# Revit family: JMv 315 - 630
name_source: partatom
category: Mechanical Equipment
revit_build: Autodesk Revit MEP 2014 (Build: 20130308_1515(x64)
units: mm (PartAtom-declared; Revit-internal decimal feet)

## types (49) — shared parameters
Air Flow Rate Supply = 0 m³/h
Blade Angle = 0.00°
Description = 0000 JM
Electrical Load (Input Power) = 0 kW
Electrical Power (Rated Power) = 0 kW
Fan Code = Model/code
Fan Diameter / Size = 0000 mm
Frequency = 50 Hz
Full Load Current = 0 A
Manufacturer = Flakt Woods Group
Material = Steel
Max Voltage = 420 V
Maximum Operating Temperature = 60 °C
Min Voltage = 380 V
Minimum Operating Temperature = -20 °C
Model = Model/code
Motor Rating = 0 kW
Mounting Feet = Yes
Organisation = Flakt Woods Group
Power = 0 kW
Protective Earth = No
Smoke Control Flow rate Extract = 0 m³/h
Smoke Control Temperature = 0 °C
Smoke Control Time = 0.0 min
Starting Current = 0 A
T/Box 12 O'clock = Yes
T/Box 3 O'clock = No
T/Box 9 O'clock = No
Total Pressure Supply = 0.00 Pa
URL = http://www.flaktwoods.com
zero-valued in all types: Annual Carbon Footprint, Blades, Breakout Sound Level - Lw dB(A), Cost, Extract Diameter, Fan Speed - RPM, Inlet Sound Level - Lw dB(A), Outlet Sound Level - Lw dB(A), Overall Height, Poles, SFP - W/(l/s), Size, Unit Height, Unit Width

## per-type parameters (varying)
| type | Dimension D | Dimension K | Dimension L | Dimension L/2 | Dimension P | Fan Radius | Feet Extrusion Start | Flange Holes | Flange Size | Hub | Overall Length | Overall Width | Smoke Control Flow rate Supply | Static Pressure Supply | Supply Diameter | Total Weight | Unit Length | Unit Weight | Velocity Supply |
| 315 BT4 | 230 mm | 285 mm  [stored 0.935039 ft] | 265 mm  [stored 0.869423 ft] | 133 mm | 200 mm  [stored 0.656168 ft] | 158 mm | -158 mm |  | 40 mm  [stored 0.131234 ft] | 0 | 1565 mm | 45 mm  [stored 0.147638 ft] | 0 m³/h | 0.00 Pa | 315 mm  [stored 1.03346 ft] | 0.00 kg | 375 mm  [stored 1.23031 ft] | 20.78 kg | 0 m/s |
| 315 BT5 | 230 mm | 285 mm  [stored 0.935039 ft] | 265 mm  [stored 0.869423 ft] | 133 mm | 200 mm  [stored 0.656168 ft] | 158 mm | -158 mm |  | 40 mm  [stored 0.131234 ft] | 0 | 1565 mm | 45 mm  [stored 0.147638 ft] | 0 m³/h | 0.00 Pa | 315 mm  [stored 1.03346 ft] | 0.00 kg | 375 mm  [stored 1.23031 ft] | 21.28 kg | 0 m/s |
| 315 BT9 | 230 mm | 285 mm  [stored 0.935039 ft] | 265 mm  [stored 0.869423 ft] | 133 mm | 200 mm  [stored 0.656168 ft] | 158 mm | -158 mm |  | 40 mm  [stored 0.131234 ft] | 0 | 1565 mm | 45 mm  [stored 0.147638 ft] | 0 m³/h | 0.00 Pa | 315 mm  [stored 1.03346 ft] | 0.00 kg | 375 mm  [stored 1.23031 ft] | 22.78 kg | 0 m/s |
| 315 CT5 | 230 mm | 285 mm  [stored 0.935039 ft] | 265 mm  [stored 0.869423 ft] | 133 mm | 200 mm  [stored 0.656168 ft] | 158 mm | -158 mm |  | 40 mm  [stored 0.131234 ft] | 0 | 1565 mm | 45 mm  [stored 0.147638 ft] | 0 m³/h | 0.00 Pa | 315 mm  [stored 1.03346 ft] | 0.00 kg | 375 mm  [stored 1.23031 ft] | 23.76 kg | 0 m/s |
| 315 CT9 | 230 mm | 285 mm  [stored 0.935039 ft] | 265 mm  [stored 0.869423 ft] | 133 mm | 200 mm  [stored 0.656168 ft] | 158 mm | -158 mm |  | 40 mm  [stored 0.131234 ft] | 0 | 1565 mm | 45 mm  [stored 0.147638 ft] | 0 m³/h | 0.00 Pa | 315 mm  [stored 1.03346 ft] | 0.00 kg | 375 mm  [stored 1.23031 ft] | 26.76 kg | 0 m/s |
| 315 80 | 230 mm | 285 mm  [stored 0.935039 ft] | 265 mm  [stored 0.869423 ft] | 133 mm | 200 mm  [stored 0.656168 ft] | 158 mm | -158 mm |  | 40 mm  [stored 0.131234 ft] | 0 | 1565 mm | 45 mm  [stored 0.147638 ft] | 0 m³/h | 0.00 Pa | 315 mm  [stored 1.03346 ft] | 0.00 kg | 375 mm  [stored 1.23031 ft] | 32.52 kg | 0 m/s |
| 355 BT4 | 250 mm  [stored 0.82021 ft] | 285 mm  [stored 0.935039 ft] | 305 mm  [stored 1.00066 ft] | 153 mm | 225 mm  [stored 0.738189 ft] | 178 mm | -178 mm |  | 40 mm  [stored 0.131234 ft] | 0 | 1565 mm | 45 mm  [stored 0.147638 ft] | 0 m³/h | 0.00 Pa | 355 mm | 0.00 kg | 375 mm  [stored 1.23031 ft] | 22.18 kg | 0 m/s |
| 355 BT5 | 250 mm  [stored 0.82021 ft] | 285 mm  [stored 0.935039 ft] | 305 mm  [stored 1.00066 ft] | 153 mm | 225 mm  [stored 0.738189 ft] | 178 mm | -178 mm |  | 40 mm  [stored 0.131234 ft] | 0 | 1565 mm | 45 mm  [stored 0.147638 ft] | 0 m³/h | 0.00 Pa | 355 mm | 0.00 kg | 375 mm  [stored 1.23031 ft] | 22.68 kg | 0 m/s |
| 355 BT9 | 250 mm  [stored 0.82021 ft] | 285 mm  [stored 0.935039 ft] | 305 mm  [stored 1.00066 ft] | 153 mm | 225 mm  [stored 0.738189 ft] | 178 mm | -178 mm |  | 40 mm  [stored 0.131234 ft] | 0 | 1565 mm | 45 mm  [stored 0.147638 ft] | 0 m³/h | 0.00 Pa | 355 mm | 0.00 kg | 375 mm  [stored 1.23031 ft] | 24.18 kg | 0 m/s |
| 355 CT5 | 250 mm  [stored 0.82021 ft] | 285 mm  [stored 0.935039 ft] | 305 mm  [stored 1.00066 ft] | 153 mm | 225 mm  [stored 0.738189 ft] | 178 mm | -178 mm |  | 40 mm  [stored 0.131234 ft] | 0 | 1565 mm | 45 mm  [stored 0.147638 ft] | 0 m³/h | 0.00 Pa | 355 mm | 0.00 kg | 375 mm  [stored 1.23031 ft] | 25.32 kg | 0 m/s |
| 355 CT9 | 250 mm  [stored 0.82021 ft] | 285 mm  [stored 0.935039 ft] | 305 mm  [stored 1.00066 ft] | 153 mm | 225 mm  [stored 0.738189 ft] | 178 mm | -178 mm |  | 40 mm  [stored 0.131234 ft] | 0 | 1565 mm | 45 mm  [stored 0.147638 ft] | 0 m³/h | 0.00 Pa | 355 mm | 0.00 kg | 375 mm  [stored 1.23031 ft] | 28.32 kg | 0 m/s |
| 355 80 | 250 mm  [stored 0.82021 ft] | 285 mm  [stored 0.935039 ft] | 305 mm  [stored 1.00066 ft] | 153 mm | 225 mm  [stored 0.738189 ft] | 178 mm | -178 mm |  | 40 mm  [stored 0.131234 ft] | 0 | 1565 mm | 45 mm  [stored 0.147638 ft] | 0 m³/h | 0.00 Pa | 355 mm | 0.00 kg | 375 mm  [stored 1.23031 ft] | 34.28 kg | 0 m/s |
| 400 BT4 | 272 mm | 285 mm  [stored 0.935039 ft] | 350 mm  [stored 1.14829 ft] | 175 mm  [stored 0.574147 ft] | 250 mm  [stored 0.82021 ft] | 200 mm  [stored 0.656168 ft] | -200 mm  [stored -0.656168 ft] |  | 40 mm  [stored 0.131234 ft] | 0 | 1565 mm | 45 mm  [stored 0.147638 ft] | 0 m³/h | 0.00 Pa | 400 mm  [stored 1.31234 ft] | 0.00 kg | 375 mm  [stored 1.23031 ft] | 23.38 kg | 0 m/s |
| 400 BT5 | 272 mm | 285 mm  [stored 0.935039 ft] | 350 mm  [stored 1.14829 ft] | 175 mm  [stored 0.574147 ft] | 250 mm  [stored 0.82021 ft] | 200 mm  [stored 0.656168 ft] | -200 mm  [stored -0.656168 ft] |  | 40 mm  [stored 0.131234 ft] | 0 | 1565 mm | 45 mm  [stored 0.147638 ft] | 0 m³/h | 0.00 Pa | 400 mm  [stored 1.31234 ft] | 0.00 kg | 375 mm  [stored 1.23031 ft] | 23.88 kg | 0 m/s |
| 400  BT9 | 272 mm | 285 mm  [stored 0.935039 ft] | 350 mm  [stored 1.14829 ft] | 175 mm  [stored 0.574147 ft] | 250 mm  [stored 0.82021 ft] | 200 mm  [stored 0.656168 ft] | -200 mm  [stored -0.656168 ft] |  | 40 mm  [stored 0.131234 ft] | 0 | 1565 mm | 45 mm  [stored 0.147638 ft] | 0 m³/h | 0.00 Pa | 400 mm  [stored 1.31234 ft] | 0.00 kg | 375 mm  [stored 1.23031 ft] | 25.38 kg | 0 m/s |
| 400 CT5 | 272 mm | 285 mm  [stored 0.935039 ft] | 350 mm  [stored 1.14829 ft] | 175 mm  [stored 0.574147 ft] | 250 mm  [stored 0.82021 ft] | 200 mm  [stored 0.656168 ft] | -200 mm  [stored -0.656168 ft] |  | 40 mm  [stored 0.131234 ft] | 0 | 1565 mm | 45 mm  [stored 0.147638 ft] | 0 m³/h | 0.00 Pa | 400 mm  [stored 1.31234 ft] | 0.00 kg | 375 mm  [stored 1.23031 ft] | 26.24 kg | 0 m/s |
| 400 CT9 | 272 mm | 285 mm  [stored 0.935039 ft] | 350 mm  [stored 1.14829 ft] | 175 mm  [stored 0.574147 ft] | 250 mm  [stored 0.82021 ft] | 200 mm  [stored 0.656168 ft] | -200 mm  [stored -0.656168 ft] |  | 40 mm  [stored 0.131234 ft] | 0 | 1565 mm | 45 mm  [stored 0.147638 ft] | 0 m³/h | 0.00 Pa | 400 mm  [stored 1.31234 ft] | 0.00 kg | 375 mm  [stored 1.23031 ft] | 29.24 kg | 0 m/s |
| 400 80 | 272 mm | 285 mm  [stored 0.935039 ft] | 350 mm  [stored 1.14829 ft] | 175 mm  [stored 0.574147 ft] | 250 mm  [stored 0.82021 ft] | 200 mm  [stored 0.656168 ft] | -200 mm  [stored -0.656168 ft] |  | 40 mm  [stored 0.131234 ft] | 0 | 1565 mm | 45 mm  [stored 0.147638 ft] | 0 m³/h | 0.00 Pa | 400 mm  [stored 1.31234 ft] | 0.00 kg | 375 mm  [stored 1.23031 ft] | 34.96 kg | 0 m/s |
| 400 90 | 272 mm | 285 mm  [stored 0.935039 ft] | 350 mm  [stored 1.14829 ft] | 175 mm  [stored 0.574147 ft] | 250 mm  [stored 0.82021 ft] | 200 mm  [stored 0.656168 ft] | -200 mm  [stored -0.656168 ft] |  | 40 mm  [stored 0.131234 ft] | 0 | 1565 mm | 45 mm  [stored 0.147638 ft] | 0 m³/h | 0.00 Pa | 400 mm  [stored 1.31234 ft] | 0.00 kg | 375 mm  [stored 1.23031 ft] | 36.52 kg | 0 m/s |
| 450 BT4 | 297 mm  [stored 0.974409 ft] | 275 mm | 400 mm  [stored 1.31234 ft] | 200 mm  [stored 0.656168 ft] | 280 mm  [stored 0.918635 ft] | 225 mm  [stored 0.738189 ft] | -225 mm  [stored -0.738189 ft] |  | 40 mm  [stored 0.131234 ft] | 0 | 1565 mm | 45 mm  [stored 0.147638 ft] | 0 m³/h | 0.00 Pa | 450 mm | 0.00 kg | 375 mm  [stored 1.23031 ft] | 24.14 kg | 0 m/s |
| 450  BT5 | 297 mm  [stored 0.974409 ft] | 275 mm | 400 mm  [stored 1.31234 ft] | 200 mm  [stored 0.656168 ft] | 280 mm  [stored 0.918635 ft] | 225 mm  [stored 0.738189 ft] | -225 mm  [stored -0.738189 ft] |  | 40 mm  [stored 0.131234 ft] | 0 | 1565 mm | 45 mm  [stored 0.147638 ft] | 0 m³/h | 0.00 Pa | 450 mm | 0.00 kg | 375 mm  [stored 1.23031 ft] | 24.64 kg | 0 m/s |
| 450 BT9 | 297 mm  [stored 0.974409 ft] | 275 mm | 400 mm  [stored 1.31234 ft] | 200 mm  [stored 0.656168 ft] | 280 mm  [stored 0.918635 ft] | 225 mm  [stored 0.738189 ft] | -225 mm  [stored -0.738189 ft] |  | 40 mm  [stored 0.131234 ft] | 0 | 1565 mm | 45 mm  [stored 0.147638 ft] | 0 m³/h | 0.00 Pa | 450 mm | 0.00 kg | 375 mm  [stored 1.23031 ft] | 26.14 kg | 0 m/s |
| 450 CT5 | 297 mm  [stored 0.974409 ft] | 275 mm | 400 mm  [stored 1.31234 ft] | 200 mm  [stored 0.656168 ft] | 280 mm  [stored 0.918635 ft] | 225 mm  [stored 0.738189 ft] | -225 mm  [stored -0.738189 ft] |  | 40 mm  [stored 0.131234 ft] | 0 | 1565 mm | 45 mm  [stored 0.147638 ft] | 0 m³/h | 0.00 Pa | 450 mm | 0.00 kg | 375 mm  [stored 1.23031 ft] | 27.24 kg | 0 m/s |
| 450 CT9 | 297 mm  [stored 0.974409 ft] | 275 mm | 400 mm  [stored 1.31234 ft] | 200 mm  [stored 0.656168 ft] | 280 mm  [stored 0.918635 ft] | 225 mm  [stored 0.738189 ft] | -225 mm  [stored -0.738189 ft] |  | 40 mm  [stored 0.131234 ft] | 0 | 755 mm | 50 mm  [stored 0.164042 ft] | 0 m³/h | 0.00 Pa | 450 mm | 0.00 kg | 375 mm  [stored 1.23031 ft] | 30.24 kg | 0 m/s |
| 450 80 | 297 mm  [stored 0.974409 ft] | 275 mm | 400 mm  [stored 1.31234 ft] | 200 mm  [stored 0.656168 ft] | 280 mm  [stored 0.918635 ft] | 225 mm  [stored 0.738189 ft] | -225 mm  [stored -0.738189 ft] |  | 40 mm  [stored 0.131234 ft] | 0 | 1565 mm | 45 mm  [stored 0.147638 ft] | 0 m³/h | 0.00 Pa | 450 mm | 0.00 kg | 375 mm  [stored 1.23031 ft] | 36.08 kg | 0 m/s |
| 450 90 | 297 mm  [stored 0.974409 ft] | 275 mm | 400 mm  [stored 1.31234 ft] | 200 mm  [stored 0.656168 ft] | 280 mm  [stored 0.918635 ft] | 225 mm  [stored 0.738189 ft] | -225 mm  [stored -0.738189 ft] |  | 40 mm  [stored 0.131234 ft] | 0 | 1565 mm | 45 mm  [stored 0.147638 ft] | 0 m³/h | 0.00 Pa | 450 mm | 0.00 kg | 375 mm  [stored 1.23031 ft] | 37.64 kg | 0 m/s |
| 500 CT5 | 322 mm  [stored 1.05643 ft] | 420 mm | 450 mm | 225 mm  [stored 0.738189 ft] | 315 mm  [stored 1.03346 ft] | 250 mm  [stored 0.82021 ft] | -250 mm  [stored -0.82021 ft] |  | 47 mm  [stored 0.154199 ft] | 0 | 1565 mm | 45 mm  [stored 0.147638 ft] | 0 m³/h | 0.00 Pa | 500 mm | 0.00 kg | 520 mm | 46.16 kg | 0 m/s |
| 500 CT9 | 322 mm  [stored 1.05643 ft] | 420 mm | 450 mm | 225 mm  [stored 0.738189 ft] | 315 mm  [stored 1.03346 ft] | 250 mm  [stored 0.82021 ft] | -250 mm  [stored -0.82021 ft] |  | 47 mm  [stored 0.154199 ft] | 0 | 1565 mm | 45 mm  [stored 0.147638 ft] | 0 m³/h | 0.00 Pa | 500 mm | 0.00 kg | 520 mm | 49.16 kg | 0 m/s |
| 500 80 | 322 mm  [stored 1.05643 ft] | 420 mm | 450 mm | 225 mm  [stored 0.738189 ft] | 315 mm  [stored 1.03346 ft] | 250 mm  [stored 0.82021 ft] | -250 mm  [stored -0.82021 ft] |  | 47 mm  [stored 0.154199 ft] | 0 | 1565 mm | 45 mm  [stored 0.147638 ft] | 0 m³/h | 0.00 Pa | 500 mm | 0.00 kg | 520 mm | 54.84 kg | 0 m/s |
| 500 90 | 322 mm  [stored 1.05643 ft] | 420 mm | 450 mm | 225 mm  [stored 0.738189 ft] | 315 mm  [stored 1.03346 ft] | 250 mm  [stored 0.82021 ft] | -250 mm  [stored -0.82021 ft] |  | 47 mm  [stored 0.154199 ft] | 0 | 1565 mm | 45 mm  [stored 0.147638 ft] | 0 m³/h | 0.00 Pa | 500 mm | 0.00 kg | 520 mm | 56.52 kg | 0 m/s |
| 500 F22 | 322 mm  [stored 1.05643 ft] | 420 mm | 450 mm | 225 mm  [stored 0.738189 ft] | 315 mm  [stored 1.03346 ft] | 250 mm  [stored 0.82021 ft] | -250 mm  [stored -0.82021 ft] |  | 47 mm  [stored 0.154199 ft] | 0 | 1565 mm | 45 mm  [stored 0.147638 ft] | 0 m³/h | 0.00 Pa | 500 mm | 0.00 kg | 520 mm | 60.24 kg | 0 m/s |
| 500 100L | 322 mm  [stored 1.05643 ft] | 420 mm | 450 mm | 225 mm  [stored 0.738189 ft] | 315 mm  [stored 1.03346 ft] | 250 mm  [stored 0.82021 ft] | -250 mm  [stored -0.82021 ft] |  | 47 mm  [stored 0.154199 ft] | 0 | 1565 mm | 45 mm  [stored 0.147638 ft] | 0 m³/h | 0.00 Pa | 500 mm | 0.00 kg | 520 mm | 68.24 kg | 0 m/s |
| 500 112M | 322 mm  [stored 1.05643 ft] | 420 mm | 450 mm | 225 mm  [stored 0.738189 ft] | 315 mm  [stored 1.03346 ft] | 250 mm  [stored 0.82021 ft] | -250 mm  [stored -0.82021 ft] |  | 47 mm  [stored 0.154199 ft] | 0 | 1565 mm | 45 mm  [stored 0.147638 ft] | 0 m³/h | 0.00 Pa | 500 mm | 0.00 kg | 520 mm | 78.16 kg | 0 m/s |
| 560 CT5 | 352 mm  [stored 1.15486 ft] | 420 mm | 510 mm | 255 mm  [stored 0.836614 ft] | 355 mm | 280 mm  [stored 0.918635 ft] | -280 mm  [stored -0.918635 ft] |  | 47 mm  [stored 0.154199 ft] | 0 | 1565 mm | 45 mm  [stored 0.147638 ft] | 0 m³/h | 0.00 Pa | 560 mm | 0.00 kg | 520 mm | 51.06 kg | 0 m/s |
| 560 CT9 | 352 mm  [stored 1.15486 ft] | 420 mm | 510 mm | 255 mm  [stored 0.836614 ft] | 355 mm | 280 mm  [stored 0.918635 ft] | -280 mm  [stored -0.918635 ft] |  | 47 mm  [stored 0.154199 ft] | 0 | 1565 mm | 45 mm  [stored 0.147638 ft] | 0 m³/h | 0.00 Pa | 560 mm | 0.00 kg | 520 mm | 54.18 kg | 0 m/s |
| 560 80 | 352 mm  [stored 1.15486 ft] | 420 mm | 510 mm | 255 mm  [stored 0.836614 ft] | 355 mm | 280 mm  [stored 0.918635 ft] | -280 mm  [stored -0.918635 ft] |  | 47 mm  [stored 0.154199 ft] | 0 | 1565 mm | 45 mm  [stored 0.147638 ft] | 0 m³/h | 0.00 Pa | 560 mm | 0.00 kg | 520 mm | 59.42 kg | 0 m/s |
| 560 90 | 352 mm  [stored 1.15486 ft] | 420 mm | 510 mm | 255 mm  [stored 0.836614 ft] | 355 mm | 280 mm  [stored 0.918635 ft] | -280 mm  [stored -0.918635 ft] |  | 47 mm  [stored 0.154199 ft] | 0 | 1565 mm | 45 mm  [stored 0.147638 ft] | 0 m³/h | 0.00 Pa | 560 mm | 0.00 kg | 520 mm | 60.94 kg | 0 m/s |
| 560 F22 | 352 mm  [stored 1.15486 ft] | 420 mm | 510 mm | 255 mm  [stored 0.836614 ft] | 355 mm | 280 mm  [stored 0.918635 ft] | -280 mm  [stored -0.918635 ft] |  | 47 mm  [stored 0.154199 ft] | 0 | 1565 mm | 45 mm  [stored 0.147638 ft] | 0 m³/h | 0.00 Pa | 560 mm | 0.00 kg | 520 mm | 64.22 kg | 0 m/s |
| 560 100L | 352 mm  [stored 1.15486 ft] | 420 mm | 510 mm | 255 mm  [stored 0.836614 ft] | 355 mm | 280 mm  [stored 0.918635 ft] | -280 mm  [stored -0.918635 ft] |  | 47 mm  [stored 0.154199 ft] | 0 | 1565 mm | 45 mm  [stored 0.147638 ft] | 0 m³/h | 0.00 Pa | 560 mm | 0.00 kg | 520 mm | 72.22 kg | 0 m/s |
| 560 112M | 352 mm  [stored 1.15486 ft] | 420 mm | 510 mm | 255 mm  [stored 0.836614 ft] | 355 mm | 280 mm  [stored 0.918635 ft] | -280 mm  [stored -0.918635 ft] |  | 47 mm  [stored 0.154199 ft] | 0 | 1565 mm | 45 mm  [stored 0.147638 ft] | 0 m³/h | 0.00 Pa | 560 mm | 0.00 kg | 520 mm | 82.54 kg | 0 m/s |
| 630 CT5 | 387 mm  [stored 1.26969 ft] | 400 mm  [stored 1.31234 ft] | 580 mm | 290 mm  [stored 0.951444 ft] | 400 mm  [stored 1.31234 ft] | 315 mm  [stored 1.03346 ft] | -315 mm  [stored -1.03346 ft] |  | 47 mm  [stored 0.154199 ft] | 0 | 1565 mm | 45 mm  [stored 0.147638 ft] | 0 m³/h | 0.00 Pa | 630 mm | 0.00 kg | 520 mm | 69.58 kg | 0 m/s |
| 630 CT9 | 387 mm  [stored 1.26969 ft] | 400 mm  [stored 1.31234 ft] | 580 mm | 290 mm  [stored 0.951444 ft] | 400 mm  [stored 1.31234 ft] | 315 mm  [stored 1.03346 ft] | -315 mm  [stored -1.03346 ft] |  | 47 mm  [stored 0.154199 ft] | 0 | 1565 mm | 45 mm  [stored 0.147638 ft] | 0 m³/h | 0.00 Pa | 630 mm | 0.00 kg | 520 mm | 72.62 kg | 0 m/s |
| 630 80 | 387 mm  [stored 1.26969 ft] | 400 mm  [stored 1.31234 ft] | 580 mm | 290 mm  [stored 0.951444 ft] | 400 mm  [stored 1.31234 ft] | 315 mm  [stored 1.03346 ft] | -315 mm  [stored -1.03346 ft] |  | 47 mm  [stored 0.154199 ft] | 0 | 1565 mm | 45 mm  [stored 0.147638 ft] | 0 m³/h | 0.00 Pa | 630 mm | 0.00 kg | 520 mm | 78.06 kg | 0 m/s |
| 630 90 | 387 mm  [stored 1.26969 ft] | 400 mm  [stored 1.31234 ft] | 580 mm | 290 mm  [stored 0.951444 ft] | 400 mm  [stored 1.31234 ft] | 315 mm  [stored 1.03346 ft] | -315 mm  [stored -1.03346 ft] |  | 47 mm  [stored 0.154199 ft] | 0 | 1565 mm | 45 mm  [stored 0.147638 ft] | 0 m³/h | 0.00 Pa | 630 mm | 0.00 kg | 520 mm | 79.66 kg | 0 m/s |
| 630 F22 | 387 mm  [stored 1.26969 ft] | 400 mm  [stored 1.31234 ft] | 580 mm | 290 mm  [stored 0.951444 ft] | 400 mm  [stored 1.31234 ft] | 315 mm  [stored 1.03346 ft] | -315 mm  [stored -1.03346 ft] |  | 47 mm  [stored 0.154199 ft] | 0 | 1565 mm | 45 mm  [stored 0.147638 ft] | 0 m³/h | 0.00 Pa | 630 mm | 0.00 kg | 520 mm | 82.82 kg | 0 m/s |
| 630 100L | 387 mm  [stored 1.26969 ft] | 400 mm  [stored 1.31234 ft] | 580 mm | 290 mm  [stored 0.951444 ft] | 400 mm  [stored 1.31234 ft] | 315 mm  [stored 1.03346 ft] | -315 mm  [stored -1.03346 ft] |  | 47 mm  [stored 0.154199 ft] | 0 | 1565 mm | 45 mm  [stored 0.147638 ft] | 0 m³/h | 0.00 Pa | 630 mm | 0.00 kg | 520 mm | 90.78 kg | 0 m/s |
| 630 112M | 387 mm  [stored 1.26969 ft] | 400 mm  [stored 1.31234 ft] | 580 mm | 290 mm  [stored 0.951444 ft] | 400 mm  [stored 1.31234 ft] | 315 mm  [stored 1.03346 ft] | -315 mm  [stored -1.03346 ft] |  | 47 mm  [stored 0.154199 ft] | 0 | 1565 mm | 45 mm  [stored 0.147638 ft] | 0 m³/h | 0.00 Pa | 630 mm | 0.00 kg | 520 mm | 101.30 kg | 0 m/s |
| HT900 132 | 555 mm | 400 mm  [stored 1.31234 ft] | 50 mm  [stored 0.164042 ft] | 25 mm  [stored 0.082021 ft] | 518 mm | 450 mm | -450 mm  [stored -1.47638 ft] | 16 | 50 mm  [stored 0.164042 ft] | 315 | 755 mm | 900 mm | 36900 m³/h | 204.00 Pa | 900 mm | 235.00 kg | 755 mm | 235.00 kg | 16 m/s |
| 400 BT9 | 272 mm | 285 mm  [stored 0.935039 ft] | 350 mm  [stored 1.14829 ft] | 175 mm  [stored 0.574147 ft] | 250 mm  [stored 0.82021 ft] | 200 mm  [stored 0.656168 ft] | -200 mm  [stored -0.656168 ft] |  | 40 mm  [stored 0.131234 ft] | 0 | 1565 mm | 45 mm  [stored 0.147638 ft] | 0 m³/h | 0.00 Pa | 400 mm  [stored 1.31234 ft] | 0.00 kg | 375 mm  [stored 1.23031 ft] | 25.38 kg | 0 m/s |

note: [stored X ft] marks values corroborated as IEEE doubles in the binary element streams (Revit-internal decimal feet)

## geometry (parser evidence)
native form markers: Extrusion x1
no freeform markers — native parametric forms only
